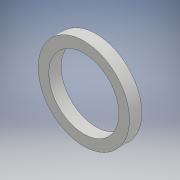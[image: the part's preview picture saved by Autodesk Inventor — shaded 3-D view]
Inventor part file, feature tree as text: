
AUTODESK INVENTOR PART (.ipt)
format: ipt  version: 2018 (Build 220112000, 112)  size: 100,864 bytes
history: native  units: mm
features: extrude x1, sketch x1
ambient origin geometry x8: Origin, YZ Plane, XZ Plane, XY Plane, X Axis, Y Axis, Z Axis, Center Point
bodies: Solid1 (feature_tree)
feature tree (2):
  extrude  "Extrusion1"  Depth=7.0mm
  sketch  "Sketch1"  dims[d0=40.0mm d1=52.0mm d2=7.0mm d3=0.0mm]
